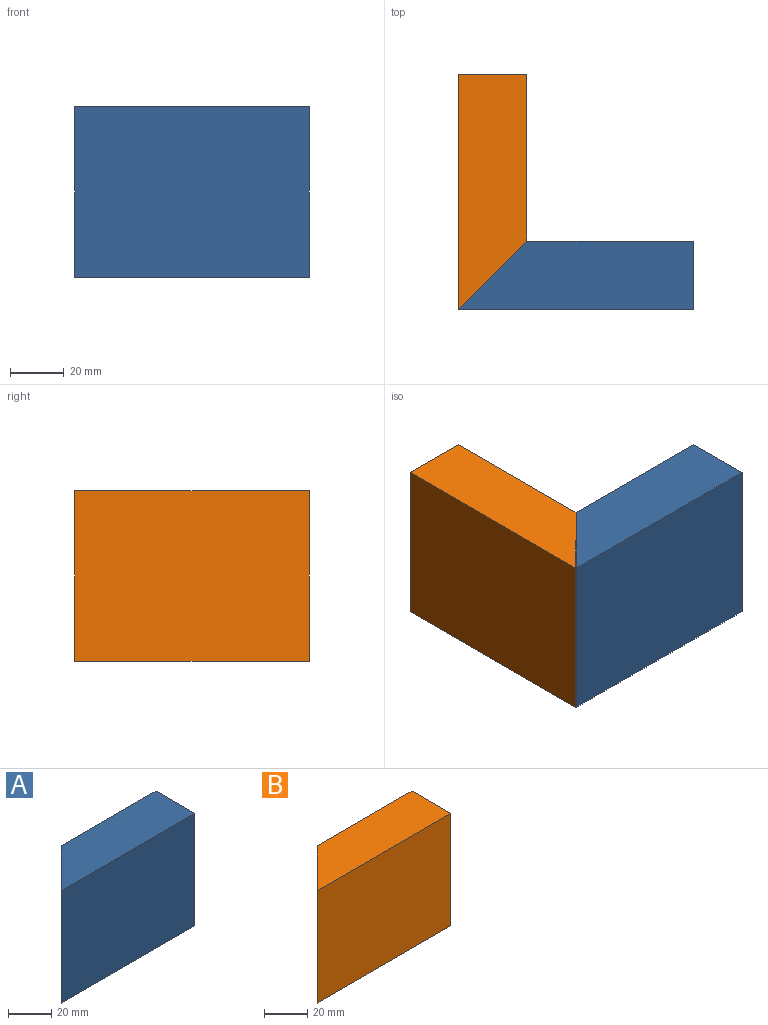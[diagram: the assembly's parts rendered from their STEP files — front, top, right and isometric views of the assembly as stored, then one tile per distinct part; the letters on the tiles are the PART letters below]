
ASSEMBLY  parts=2 mates=1
PART A: 6 faces, bbox 87.4x25.4x63.5 mm
  f0: plane 63.5x62.01mm, normal (0,1,0), area 3937.7mm2, adj f1,f3,f4,f5
  f1: plane 63.5x25.4mm, normal (-0.71,0.71,0), area 2281mm2, adj f0,f2,f4,f5
  f2: plane 87.41x63.5mm, normal (0,-1,0), area 5550.6mm2, adj f1,f3,f4,f5
  f3: plane 63.5x25.4mm, normal (1,0,0), area 1612.9mm2, adj f0,f2,f4,f5
  f4: plane 87.41x25.4mm, normal (0,0,1), area 1897.6mm2, adj f0,f1,f2,f3
  f5: plane 87.41x25.4mm, normal (0,0,-1), area 1897.6mm2, adj f0,f1,f2,f3
PART B: 6 faces, bbox 87.4x25.4x63.5 mm
  f0: plane 63.5x62.01mm, normal (0,1,0), area 3937.7mm2, adj f1,f3,f4,f5
  f1: plane 63.5x25.4mm, normal (-0.71,0.71,0), area 2281mm2, adj f0,f2,f4,f5
  f2: plane 87.41x63.5mm, normal (0,-1,0), area 5550.6mm2, adj f1,f3,f4,f5
  f3: plane 63.5x25.4mm, normal (1,0,0), area 1612.9mm2, adj f0,f2,f4,f5
  f4: plane 87.41x25.4mm, normal (0,0,1), area 1897.6mm2, adj f0,f1,f2,f3
  f5: plane 87.41x25.4mm, normal (0,0,-1), area 1897.6mm2, adj f0,f1,f2,f3
PLACE A t=(-62.75,36.58,-14.85)mm
PLACE B rot(axis=(-0.71,-0.71,0),180deg) t=(33,61.98,74.05)mm
MATE fastened B.f1 <-> A.f1  axis (0.71,-0.71,0) through (-50.05,49.28,16.9)mm
